# Revit family: Accessory-Security-HanwhaTechwin-Cover-SPB-VAN3_mm
name_source: partatom
category: Security Devices
revit_build: Autodesk Revit 2016 (Build: 20151007_0715(x64)
units: mm (PartAtom-declared; Revit-internal decimal feet)

## family parameters
Cut with Voids When Loaded = No
Host = Face
Maintain Annotation Orientation = Yes
OmniClass Number = 23.85.30.17.14
OmniClass Title = Video Surveillance
Part Type = Normal
Room Calculation Point = No
Round Connector Dimension = Use Diameter
Shared = No

## types (1)
- Standard
    Default Elevation = 1219.2 mm  [stored 4 ft]
    Description = NBS standard template for generic face-based components
    Manufacturer = HanwhaTechwinn
    Model = SPB-VAN3
    Product Documentation Link = https://www.hanwha-security.com
    Product Page URL = https://www.hanwha-security.com
    URL = https://www.hanwha-security.com

note: [stored X ft] marks values corroborated as IEEE doubles in the binary element streams (Revit-internal decimal feet)

## geometry (parser evidence)
native form markers: Sweep x2
no freeform markers — native parametric forms only
